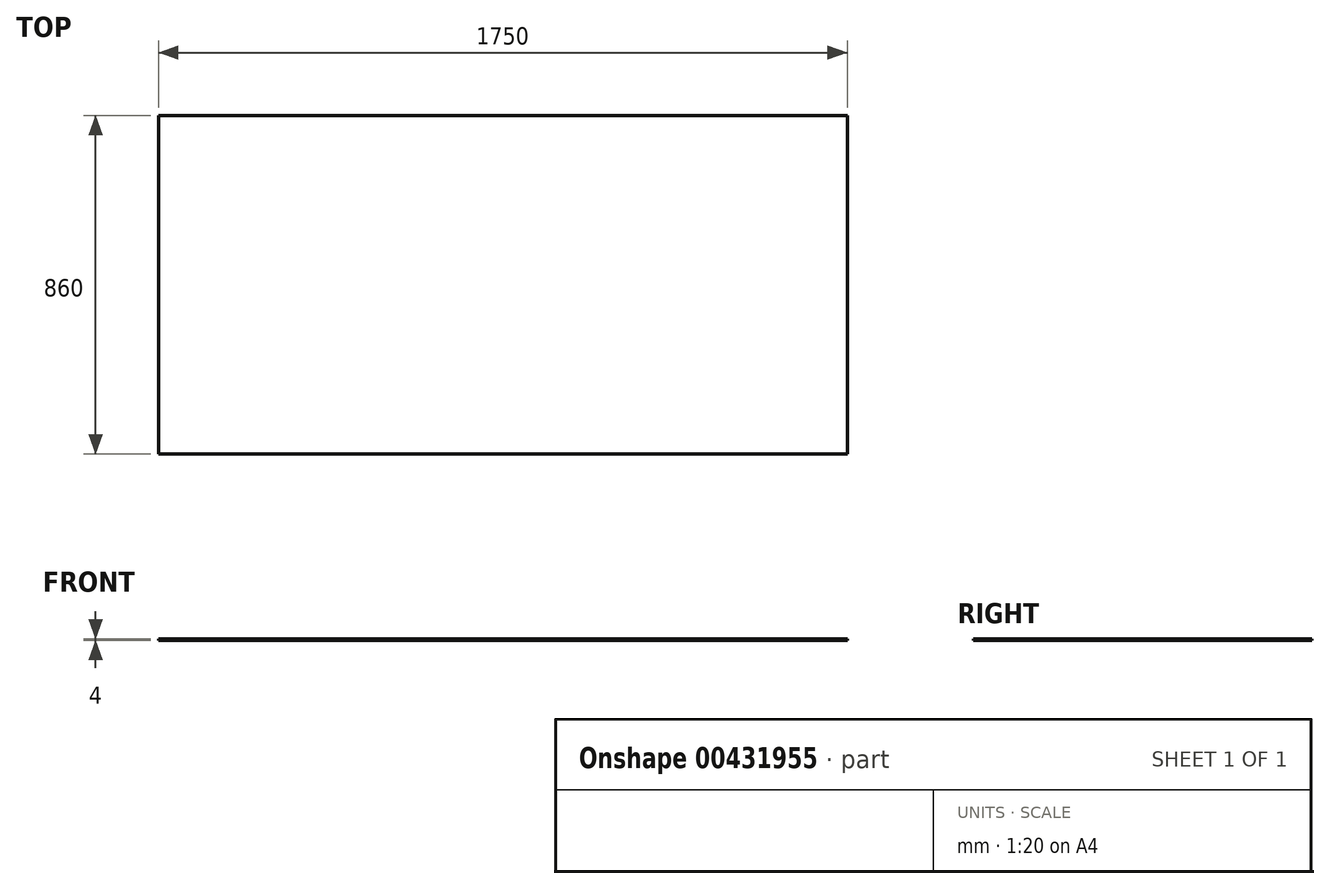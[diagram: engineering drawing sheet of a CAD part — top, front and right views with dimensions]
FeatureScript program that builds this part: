
annotation { "Feature Type Name" : "Feature", "Feature Type Description" : "" }
export const myFeature = defineFeature(function(context is Context, id is Id, definition is map)
    precondition{}
    {
        {
            var Q0;
            Q0=qCreatedBy(makeId("Top.planeOp"),FACE);
            var sketch = newSketch(context, id + "F0", { "sketchPlane" : qUnion([Q0])});
            skLineSegment(sketch, "E0.bottom", {"start": v(-875, 430) * mm, "end": v(875, 430) * mm});
            skLineSegment(sketch, "E0.top", {"start": v(-875, -430) * mm, "end": v(875, -430) * mm});
            skLineSegment(sketch, "E0.left", {"start": v(-875, 430) * mm, "end": v(-875, -430) * mm});
            skLineSegment(sketch, "E0.right", {"start": v(875, 430) * mm, "end": v(875, -430) * mm});
            skPoint(sketch, "E0.middle", {"position": v(0, 0) * mm});
            skSolve(sketch);
        }
        {
            var Q0;
            Q0 = qSketchRegion(id + "F0", true);
            extrude(context, id + "F1", {"entities" : qUnion([Q0]), "offsetDistance" : 25 * mm, "depth" : 4 * mm});
        }
    });
